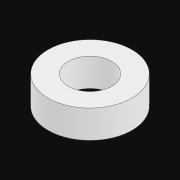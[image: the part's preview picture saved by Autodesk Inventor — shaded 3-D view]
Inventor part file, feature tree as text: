
AUTODESK INVENTOR PART (.ipt)
format: ipt  version: 2021.3 (Build 253353010, 353A)  size: 111,616 bytes
history: native  units: in
note: dims shown in document units (in); Inventor stores cm internally (conversion verified against a paired STEP export)
features: other x5, extrude x1, sketch x1
ambient origin geometry x8: Origin, YZ Plane, XZ Plane, XY Plane, X Axis, Y Axis, Z Axis, Center Point
bodies: Solid1 (feature_tree)
feature tree (7):
  other  "Table"
  other  "NSpacer .313 OD x .125"
  other  "NSpacer .313 OD x .250"
  other  "NSpacer .313 OD x .375"
  other  "NSpacer .313 OD x .500"
  extrude  "Extrusion1"  Depth=0.375in
  sketch  "Sketch1"  dims[d0=0.194in d1=0.375in d3=0.0in]
